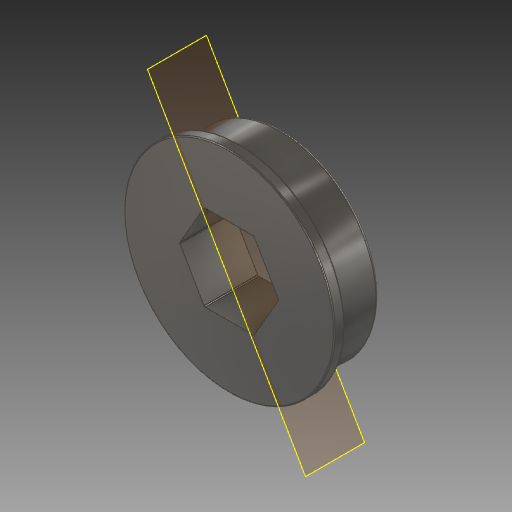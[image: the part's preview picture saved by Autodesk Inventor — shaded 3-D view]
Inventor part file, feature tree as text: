
AUTODESK INVENTOR PART (.ipt)
format: ipt  version: 2017.1 (Build 211199000, 199)  size: 167,936 bytes
history: native  units: in
note: dims shown in document units (in); Inventor stores cm internally (conversion verified against a paired STEP export)
features: plane x1, fillet x1
ambient origin geometry x8: Origin, YZ Plane, XZ Plane, XY Plane, X Axis, Y Axis, Z Axis, Center Point
bodies: Solid1 (feature_tree)
feature tree (2):
  plane  "Work Plane1"
  fillet  "Fillet2"  [1 undecoded]
note: 1 required parameter value undecoded (feature->parameter linkage not recoverable at this tier; creation-order binding heuristic only, values carry confidence <= 0.55)
